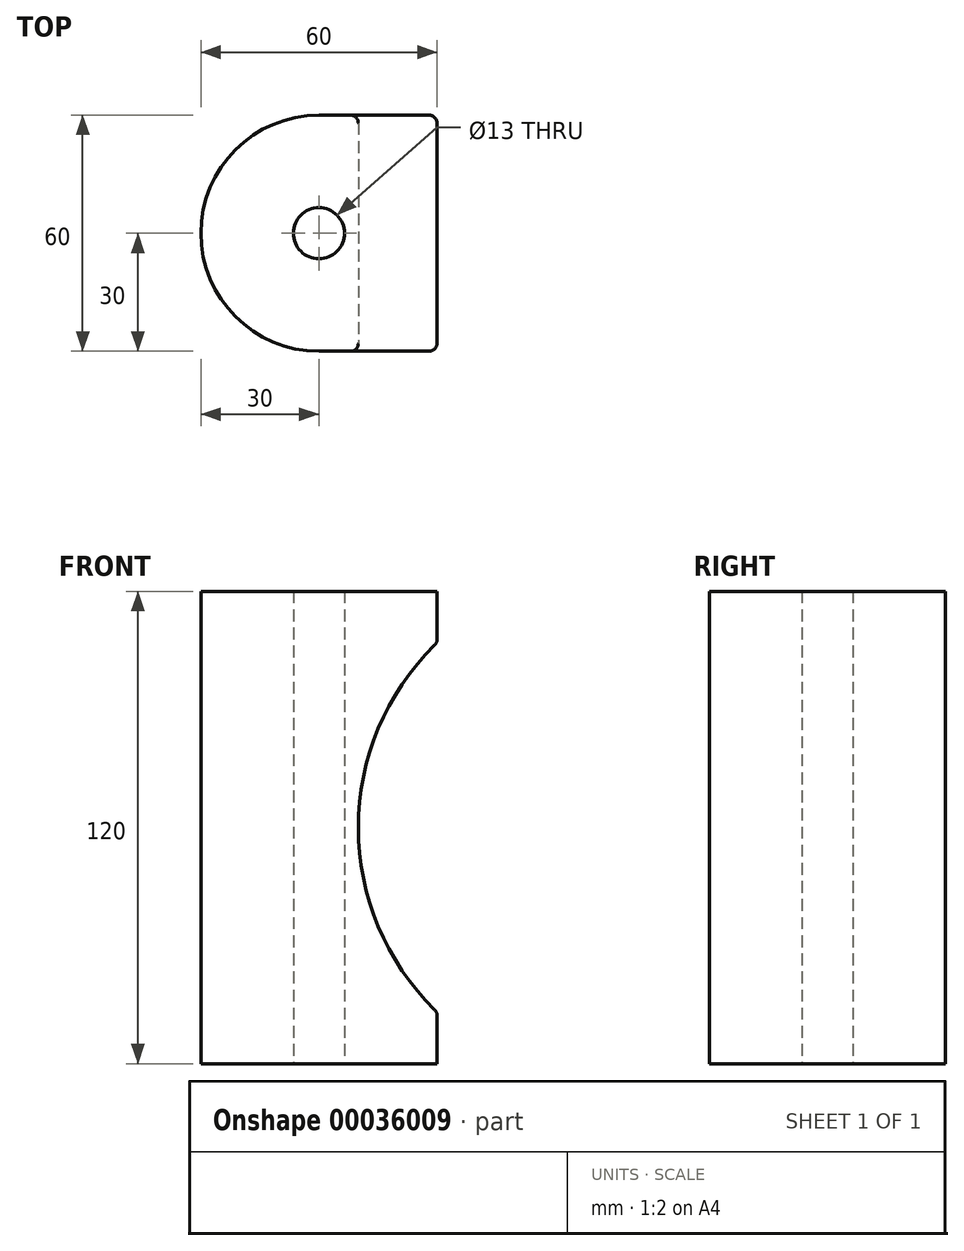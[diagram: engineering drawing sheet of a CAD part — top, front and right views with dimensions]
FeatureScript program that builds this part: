
annotation { "Feature Type Name" : "Feature", "Feature Type Description" : "" }
export const myFeature = defineFeature(function(context is Context, id is Id, definition is map)
    precondition{}
    {
        {
            var Q0;
            Q0=qCreatedBy(makeId("Top.planeOp"),FACE);
            var sketch = newSketch(context, id + "F0", { "sketchPlane" : qUnion([Q0])});
            skLineSegment(sketch, "E0", {"start": v(0, 30) * mm, "end": v(30, 30) * mm});
            skLineSegment(sketch, "E1", {"start": v(30, 30) * mm, "end": v(30, 0) * mm});
            skCircle(sketch, "E2", {"center": v(0, 0) * mm, "radius": 30 * mm});
            skLineSegment(sketch, "E3.MirrorCS", {"start": v(30, -30) * mm, "end": v(30, 0) * mm});
            skLineSegment(sketch, "E4.MirrorCS", {"start": v(0, -30) * mm, "end": v(30, -30) * mm});
            skCircle(sketch, "E5", {"center": v(0, 0) * mm, "radius": 6.5 * mm});
            skSolve(sketch);
        }
        {
            var Q0;
            {var subQ2=sQuery(id+"F0.wireOp",EDGE,"E0");Q0=makeQuery(id+"F0.imprint","IMPRINT",FACE,{"disambiguationData":[TD([[makeQuery(id+"F0.imprint","IMPRINT",EDGE,{"derivedFrom":subQ2}),-1.0]])]});}
            var Q1;
            Q1=makeQuery(id+"F0.imprint","IMPRINT",FACE,{"disambiguationData":[TD([[makeQuery(id+"F0.imprint","IMPRINT",EDGE,{"derivedFrom":sQuery(id+"F0.wireOp",EDGE,"E5")}),-1.0]])]});
            var Q2;
            {var subQ2=sQuery(id+"F0.wireOp",EDGE,"E3.MirrorCS");Q2=makeQuery(id+"F0.imprint","IMPRINT",FACE,{"disambiguationData":[TD([[makeQuery(id+"F0.imprint","IMPRINT",EDGE,{"derivedFrom":subQ2}),1.0]])]});}
            extrude(context, id + "F1", {"entities" : qUnion([Q0, Q1, Q2]), "endBound" : BoundingType.SYMMETRIC, "depth" : 120 * mm});
        }
        {
            var Q0;
            Q0=qCreatedBy(makeId("Front.planeOp"),FACE);
            var sketch = newSketch(context, id + "F2", { "sketchPlane" : qUnion([Q0])});
            skLineSegment(sketch, "E6", {"start": v(0, 0) * mm, "end": v(75, 0) * mm, "construction": true});
            skCircle(sketch, "E7", {"center": v(75, 0) * mm, "radius": 65 * mm});
            skSolve(sketch);
        }
        {
            var Q0;
            Q0=makeQuery(id+"F2.imprint","IMPRINT",FACE,{"disambiguationData":[TD([[makeQuery(id+"F2.imprint","IMPRINT",EDGE,{"derivedFrom":sQuery(id+"F2.wireOp",EDGE,"E7")}),1.0]])]});
            extrude(context, id + "F3", {"entities" : qUnion([Q0]), "operationType" : NewBodyOperationType.REMOVE, "endBound" : BoundingType.SYMMETRIC, "oppositeDirection" : true, "depth" : 120 * mm});
        }
        {
            var Q0;
            Q0=makeQuery(id+"F3.boolean.opBoolean","INTERSECT",EDGE,{"derivedFrom":[makeQuery(id+"F1.opExtrude","SWEPT_FACE",FACE,{"disambiguationData":[OSD([sQuery(id+"F0.wireOp",EDGE,"E4.MirrorCS")])]}),makeQuery(id+"F3.opExtrude","SWEPT_FACE",FACE,{"disambiguationData":[OSD([sQuery(id+"F2.wireOp",EDGE,"E7")])]})]});
            var Q1;
            {var subQ0=sQuery(id+"F0.wireOp",EDGE,"E3.MirrorCS");var subQ1=sQuery(id+"F0.wireOp",EDGE,"E4.MirrorCS");var subQ2=sQuery(id+"F0.wireOp",EDGE,"E1");Q1=makeQuery(id+"F3.boolean.opBoolean","SPLIT",EDGE,{"disambiguationData":[TD([makeQuery(id+"F1.opExtrude","CAP_FACE",FACE,{"disambiguationData":[OSD([sQuery(id+"F0.wireOp",EDGE,"E0"),subQ2,subQ0,subQ1,sQuery(id+"F0.wireOp",EDGE,"E2"),sQuery(id+"F0.wireOp",EDGE,"E5")])],"isStart":false})])],"derivedFrom":makeQuery(id+"F1.opExtrude","SWEPT_EDGE",EDGE,{"disambiguationData":[OSD([subQ0,subQ1])]})});}
            var Q2;
            Q2=makeQuery(id+"F3.boolean.opBoolean","INTERSECT",EDGE,{"disambiguationData":[OD(1.0)],"derivedFrom":[makeQuery(id+"F1.opExtrude","SWEPT_FACE",FACE,{"disambiguationData":[OSD([sQuery(id+"F0.wireOp",EDGE,"E1"),sQuery(id+"F0.wireOp",EDGE,"E3.MirrorCS")])]}),makeQuery(id+"F3.opExtrude","SWEPT_FACE",FACE,{"disambiguationData":[OSD([sQuery(id+"F2.wireOp",EDGE,"E7")])]})]});
            var Q3;
            {var subQ0=sQuery(id+"F0.wireOp",EDGE,"E0");var subQ1=sQuery(id+"F0.wireOp",EDGE,"E1");var subQ2=sQuery(id+"F0.wireOp",EDGE,"E3.MirrorCS");Q3=makeQuery(id+"F3.boolean.opBoolean","SPLIT",EDGE,{"disambiguationData":[TD([makeQuery(id+"F1.opExtrude","CAP_FACE",FACE,{"disambiguationData":[OSD([subQ0,subQ1,subQ2,sQuery(id+"F0.wireOp",EDGE,"E4.MirrorCS"),sQuery(id+"F0.wireOp",EDGE,"E2"),sQuery(id+"F0.wireOp",EDGE,"E5")])],"isStart":false})])],"derivedFrom":makeQuery(id+"F1.opExtrude","SWEPT_EDGE",EDGE,{"disambiguationData":[OSD([subQ0,subQ1])]})});}
            var Q4;
            Q4=makeQuery(id+"F3.boolean.opBoolean","INTERSECT",EDGE,{"derivedFrom":[makeQuery(id+"F1.opExtrude","SWEPT_FACE",FACE,{"disambiguationData":[OSD([sQuery(id+"F0.wireOp",EDGE,"E0")])]}),makeQuery(id+"F3.opExtrude","SWEPT_FACE",FACE,{"disambiguationData":[OSD([sQuery(id+"F2.wireOp",EDGE,"E7")])]})]});
            var Q5;
            Q5=makeQuery(id+"F3.boolean.opBoolean","INTERSECT",EDGE,{"disambiguationData":[OD(0.0)],"derivedFrom":[makeQuery(id+"F1.opExtrude","SWEPT_FACE",FACE,{"disambiguationData":[OSD([sQuery(id+"F0.wireOp",EDGE,"E1"),sQuery(id+"F0.wireOp",EDGE,"E3.MirrorCS")])]}),makeQuery(id+"F3.opExtrude","SWEPT_FACE",FACE,{"disambiguationData":[OSD([sQuery(id+"F2.wireOp",EDGE,"E7")])]})]});
            var Q6;
            {var subQ0=sQuery(id+"F0.wireOp",EDGE,"E3.MirrorCS");var subQ1=sQuery(id+"F0.wireOp",EDGE,"E4.MirrorCS");var subQ2=sQuery(id+"F0.wireOp",EDGE,"E1");Q6=makeQuery(id+"F3.boolean.opBoolean","SPLIT",EDGE,{"disambiguationData":[TD([makeQuery(id+"F1.opExtrude","CAP_FACE",FACE,{"disambiguationData":[OSD([sQuery(id+"F0.wireOp",EDGE,"E0"),subQ2,subQ0,subQ1,sQuery(id+"F0.wireOp",EDGE,"E2"),sQuery(id+"F0.wireOp",EDGE,"E5")])],"isStart":true})])],"derivedFrom":makeQuery(id+"F1.opExtrude","SWEPT_EDGE",EDGE,{"disambiguationData":[OSD([subQ0,subQ1])]})});}
            var Q7;
            {var subQ0=sQuery(id+"F0.wireOp",EDGE,"E0");var subQ1=sQuery(id+"F0.wireOp",EDGE,"E1");var subQ2=sQuery(id+"F0.wireOp",EDGE,"E3.MirrorCS");Q7=makeQuery(id+"F3.boolean.opBoolean","SPLIT",EDGE,{"disambiguationData":[TD([makeQuery(id+"F1.opExtrude","CAP_FACE",FACE,{"disambiguationData":[OSD([subQ0,subQ1,subQ2,sQuery(id+"F0.wireOp",EDGE,"E4.MirrorCS"),sQuery(id+"F0.wireOp",EDGE,"E2"),sQuery(id+"F0.wireOp",EDGE,"E5")])],"isStart":true})])],"derivedFrom":makeQuery(id+"F1.opExtrude","SWEPT_EDGE",EDGE,{"disambiguationData":[OSD([subQ0,subQ1])]})});}
            fillet(context, id + "F4", {"entities" : qUnion([Q0, Q1, Q2, Q3, Q4, Q5, Q6, Q7]), "radius" : 2 * mm, "tangentPropagation" : true, "allowEdgeOverflow" : false});
        }
    });
